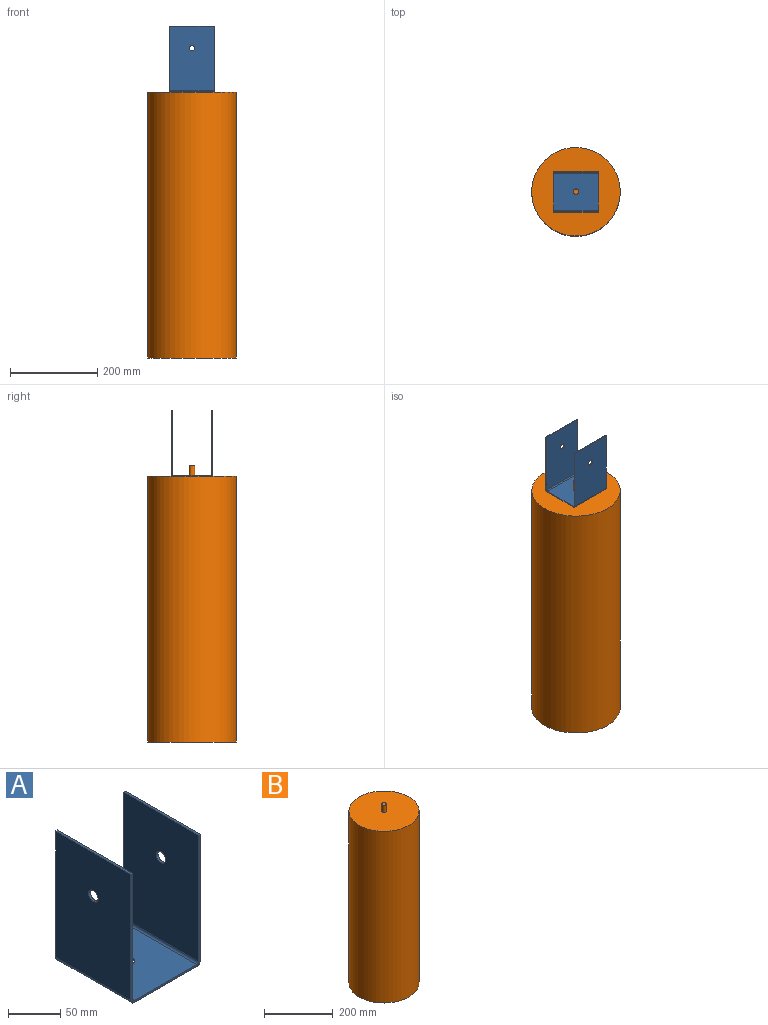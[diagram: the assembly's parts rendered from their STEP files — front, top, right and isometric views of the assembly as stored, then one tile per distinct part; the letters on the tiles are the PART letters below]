
ASSEMBLY  parts=2 mates=1
PART A: 25 faces, bbox 93.6x101.6x152.4 mm
  f0: plane 84.33x2.35mm, normal (0,1,0), area 198.1mm2, adj f3,f4,f12,f22
  f1: plane 84.33x2.35mm, normal (0,-1,0), area 198.1mm2, adj f3,f4,f11,f21
  f2: cylinder r=6.35mm len=12.7mm, axis (0,0,1), area 93.7mm2, adj f3,f4
  f3: plane 101.6x84.33mm, normal (0,0,-1), area 8441mm2, adj f0,f1,f2,f13,f23
  f4: plane 101.6x84.33mm, normal (0,0,1), area 8441mm2, adj f0,f1,f2,f14,f24
  f5: plane 101.6x2.35mm, normal (0,0,1), area 238.7mm2, adj f6,f8,f9,f10
  f6: plane 147.76x2.35mm, normal (0,-1,0), area 347.2mm2, adj f5,f9,f10,f11
  f7: cylinder r=6.35mm len=12.7mm, axis (1,0,0), area 93.7mm2, adj f9,f10
  f8: plane 147.76x2.35mm, normal (0,1,0), area 347.2mm2, adj f5,f9,f10,f12
  f9: plane 147.76x101.6mm, normal (1,0,0), area 14886.2mm2, adj f5,f6,f7,f8,f13
  f10: plane 147.76x101.6mm, normal (-1,0,0), area 14886.2mm2, adj f5,f6,f7,f8,f14
  f11: plane 4.64x4.64mm, normal (0,-1,0), area 12.8mm2, adj f1,f6,f13,f14
  f12: plane 4.64x4.64mm, normal (0,1,0), area 12.8mm2, adj f0,f8,f13,f14
  f13: cylinder r=4.64mm len=101.6mm, axis (0,-1,0), area 739.8mm2, adj f3,f9,f11,f12
  f14: cylinder r=2.29mm len=101.6mm, axis (0,-1,0), area 364.8mm2, adj f4,f10,f11,f12
  f15: plane 101.6x2.35mm, normal (0,0,1), area 238.7mm2, adj f16,f18,f19,f20
  f16: plane 147.76x2.35mm, normal (0,1,0), area 347.2mm2, adj f15,f19,f20,f22
  f17: cylinder r=6.35mm len=12.7mm, axis (-1,0,0), area 93.7mm2, adj f19,f20
  f18: plane 147.76x2.35mm, normal (0,-1,0), area 347.2mm2, adj f15,f19,f20,f21
  f19: plane 147.76x101.6mm, normal (-1,0,0), area 14886.2mm2, adj f15,f16,f17,f18,f23
  f20: plane 147.76x101.6mm, normal (1,0,0), area 14886.2mm2, adj f15,f16,f17,f18,f24
  f21: plane 4.64x4.64mm, normal (0,-1,0), area 12.8mm2, adj f1,f18,f23,f24
  f22: plane 4.64x4.64mm, normal (0,1,0), area 12.8mm2, adj f0,f16,f23,f24
  f23: cylinder r=4.64mm len=101.6mm, axis (0,-1,0), area 739.8mm2, adj f3,f19,f21,f22
  f24: cylinder r=2.29mm len=101.6mm, axis (0,-1,0), area 364.8mm2, adj f4,f20,f21,f22
PART B: 5 faces, bbox 203.2x203.2x635 mm
  f0: cylinder r=101.6mm len=609.6mm, axis (0,0,-1), area 389151.3mm2, adj f1,f2
  f1: plane 203.2x203.2mm, normal (0,0,1), area 32302.6mm2, adj f0,f3
  f2: plane 203.2x203.2mm, normal (0,0,-1), area 32429.3mm2, adj f0
  f3: cylinder r=6.35mm len=25.4mm, axis (0,0,-1), area 1013.4mm2, adj f1,f4
  f4: plane 12.7x12.7mm, normal (0,0,1), area 126.7mm2, adj f3
PLACE A rot(axis=(0,0,-1),90deg) t=(411.93,394.87,283.27)mm
PLACE B t=(411.93,394.87,-326.33)mm
MATE fastened B.f0 <-> A.f2  axis (0,0,1) through (411.93,394.87,283.27)mm
